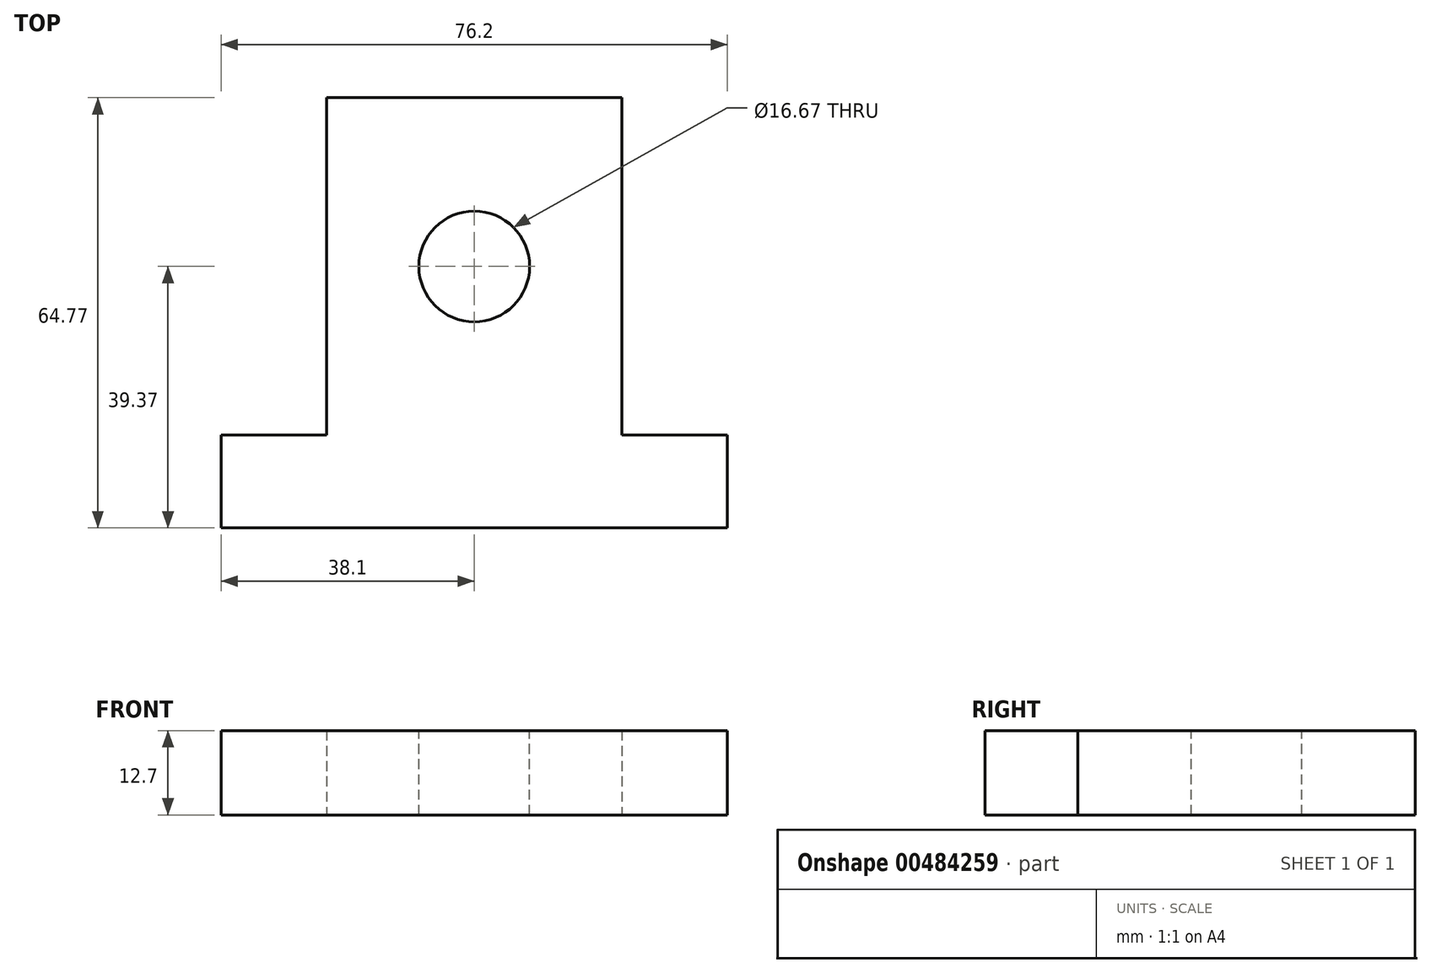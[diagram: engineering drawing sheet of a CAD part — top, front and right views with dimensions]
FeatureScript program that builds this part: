
annotation { "Feature Type Name" : "Feature", "Feature Type Description" : "" }
export const myFeature = defineFeature(function(context is Context, id is Id, definition is map)
    precondition{}
    {
        {
            var Q0;
            Q0=qCreatedBy(makeId("Top.planeOp"),FACE);
            var sketch = newSketch(context, id + "F0", { "sketchPlane" : qUnion([Q0])});
            skLineSegment(sketch, "E0.bottom", {"start": v(22.23, 25.4) * mm, "end": v(-22.23, 25.4) * mm});
            skLineSegment(sketch, "E0.left", {"start": v(22.23, 25.4) * mm, "end": v(22.23, -25.4) * mm});
            skLineSegment(sketch, "E0.right", {"start": v(-22.23, 25.4) * mm, "end": v(-22.23, -25.4) * mm});
            skPoint(sketch, "E0.middle", {"position": v(0, 0) * mm});
            skLineSegment(sketch, "E1.bottom", {"start": v(-38.1, -25.4) * mm, "end": v(-22.23, -25.4) * mm});
            skLineSegment(sketch, "E1.top", {"start": v(-38.1, -39.37) * mm, "end": v(38.1, -39.37) * mm});
            skLineSegment(sketch, "E1.left", {"start": v(-38.1, -25.4) * mm, "end": v(-38.1, -39.37) * mm});
            skLineSegment(sketch, "E1.right", {"start": v(38.1, -25.4) * mm, "end": v(38.1, -39.37) * mm});
            skLineSegment(sketch, "E2.trimOffspring", {"start": v(22.23, -25.4) * mm, "end": v(38.1, -25.4) * mm});
            skSolve(sketch);
        }
        {
            var Q0;
            Q0=makeQuery(id+"F0.imprint","IMPRINT",FACE,{"disambiguationData":[TD([[makeQuery(id+"F0.imprint","IMPRINT",EDGE,{"derivedFrom":sQuery(id+"F0.wireOp",EDGE,"E0.bottom")}),1.0]])]});
            extrude(context, id + "F1", {"entities" : qUnion([Q0]), "depth" : 12.7 * mm});
        }
        {
            var Q0;
            Q0=makeQuery(id+"F1.opExtrude","CAP_FACE",FACE,{"disambiguationData":[OSD([sQuery(id+"F0.wireOp",EDGE,"E0.bottom"),sQuery(id+"F0.wireOp",EDGE,"E0.left"),sQuery(id+"F0.wireOp",EDGE,"E0.right"),sQuery(id+"F0.wireOp",EDGE,"E1.bottom"),sQuery(id+"F0.wireOp",EDGE,"E1.top"),sQuery(id+"F0.wireOp",EDGE,"E1.left"),sQuery(id+"F0.wireOp",EDGE,"E1.right"),sQuery(id+"F0.wireOp",EDGE,"E2.trimOffspring")])],"isStart":false});
            var sketch = newSketch(context, id + "F2", { "sketchPlane" : qUnion([Q0])});
            skPoint(sketch, "E3", {"position": v(0, 0) * mm});
            skSolve(sketch);
        }
        {
            var Q0;
            Q0=sQuery(id+"F2.wireOp",VERTEX,"E3");
            var Q1;
            Q1=makeQuery(id+"F1.opExtrude","SWEPT_BODY",BODY,{"disambiguationData":[OSD([sQuery(id+"F0.wireOp",EDGE,"E0.bottom"),sQuery(id+"F0.wireOp",EDGE,"E0.left"),sQuery(id+"F0.wireOp",EDGE,"E0.right"),sQuery(id+"F0.wireOp",EDGE,"E1.bottom"),sQuery(id+"F0.wireOp",EDGE,"E1.top"),sQuery(id+"F0.wireOp",EDGE,"E1.left"),sQuery(id+"F0.wireOp",EDGE,"E1.right"),sQuery(id+"F0.wireOp",EDGE,"E2.trimOffspring")])]});
            hole(context, id + "F3", {"style" : HoleStyle.SIMPLE, "endStyle" : HoleEndStyle.THROUGH, "standardTappedOrClearance" : lookupTablePath({ "standard" : "ANSI", "fit" : "Normal (ASME)", "size" : "5/8", "type" : "Clearance" }), "standardBlindInLast" : lookupTablePath({ "fit" : "Free", "standard" : "ANSI", "size" : "5/8", "type" : "Clearance" }), "holeDiameter" : 16.67 * mm, "isTappedThrough" : true, "tappedDepth" : 12.7 * mm, "tapClearance" : 3, "locations" : qUnion([Q0]), "scope" : qUnion([Q1])});
        }
    });
